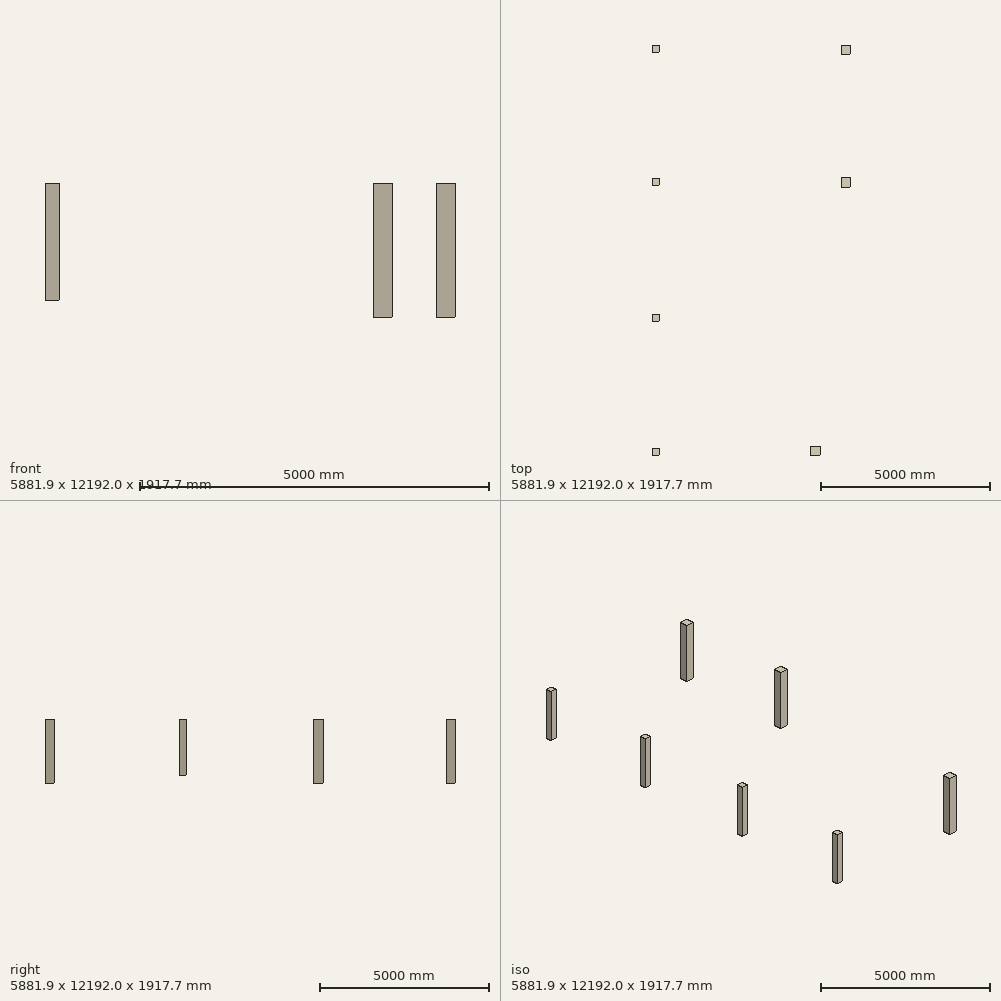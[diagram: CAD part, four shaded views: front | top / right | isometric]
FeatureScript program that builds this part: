
annotation { "Feature Type Name" : "Feature", "Feature Type Description" : "" }
export const myFeature = defineFeature(function(context is Context, id is Id, definition is map)
    precondition{}
    {
        {
            var Q0;
            Q0=qCreatedBy(makeId("Top.planeOp"),FACE);
            var sketch = newSketch(context, id + "F0", { "sketchPlane" : qUnion([Q0])});
            skLineSegment(sketch, "E0.bottom", {"start": v(0, 0) * mm, "end": v(203.2, 0) * mm});
            skLineSegment(sketch, "E0.top", {"start": v(0, 203.2) * mm, "end": v(203.2, 203.2) * mm});
            skLineSegment(sketch, "E0.left", {"start": v(0, 0) * mm, "end": v(0, 203.2) * mm});
            skLineSegment(sketch, "E0.right", {"start": v(203.2, 0) * mm, "end": v(203.2, 203.2) * mm});
            skSolve(sketch);
        }
        {
            var Q0;
            Q0=makeQuery(id+"F0.imprint","IMPRINT",FACE,{"disambiguationData":[TD([[makeQuery(id+"F0.imprint","IMPRINT",EDGE,{"derivedFrom":sQuery(id+"F0.wireOp",EDGE,"E0.bottom")}),1.0]])]});
            extrude(context, id + "F1", {"entities" : qUnion([Q0]), "depth" : 1676.4 * mm, "offsetDistance" : 25.4 * mm});
        }
        {
            var Q0;
            Q0=makeQuery(id+"F1.opExtrude","CAP_FACE",FACE,{"disambiguationData":[OSD([sQuery(id+"F0.wireOp",EDGE,"E0.bottom"),sQuery(id+"F0.wireOp",EDGE,"E0.top"),sQuery(id+"F0.wireOp",EDGE,"E0.left"),sQuery(id+"F0.wireOp",EDGE,"E0.right")])],"isStart":false});
            var sketch = newSketch(context, id + "F2", { "sketchPlane" : qUnion([Q0])});
            skLineSegment(sketch, "E1.bottom", {"start": v(0, 11988.8) * mm, "end": v(203.2, 11988.8) * mm});
            skLineSegment(sketch, "E1.top", {"start": v(0, 12192) * mm, "end": v(203.2, 12192) * mm});
            skLineSegment(sketch, "E1.left", {"start": v(0, 11988.8) * mm, "end": v(0, 12192) * mm});
            skLineSegment(sketch, "E1.right", {"start": v(203.2, 11988.8) * mm, "end": v(203.2, 12192) * mm});
            skSolve(sketch);
        }
        {
            var Q0;
            Q0=makeQuery(id+"F2.imprint","IMPRINT",FACE,{"disambiguationData":[TD([[makeQuery(id+"F2.imprint","IMPRINT",EDGE,{"derivedFrom":sQuery(id+"F2.wireOp",EDGE,"E1.bottom")}),1.0]])]});
            extrude(context, id + "F3", {"entities" : qUnion([Q0]), "oppositeDirection" : true, "depth" : 1676.4 * mm, "offsetDistance" : 25.4 * mm});
        }
        {
            var Q0;
            Q0=makeQuery(id+"F1.opExtrude","CAP_FACE",FACE,{"disambiguationData":[OSD([sQuery(id+"F0.wireOp",EDGE,"E0.bottom"),sQuery(id+"F0.wireOp",EDGE,"E0.top"),sQuery(id+"F0.wireOp",EDGE,"E0.left"),sQuery(id+"F0.wireOp",EDGE,"E0.right")])],"isStart":false});
            var sketch = newSketch(context, id + "F4", { "sketchPlane" : qUnion([Q0])});
            skLineSegment(sketch, "E2.bottom", {"start": v(0, 3975.1) * mm, "end": v(203.2, 3975.1) * mm});
            skLineSegment(sketch, "E2.top", {"start": v(0, 4178.3) * mm, "end": v(203.2, 4178.3) * mm});
            skLineSegment(sketch, "E2.left", {"start": v(0, 3975.1) * mm, "end": v(0, 4178.3) * mm});
            skLineSegment(sketch, "E2.right", {"start": v(203.2, 3975.1) * mm, "end": v(203.2, 4178.3) * mm});
            skSolve(sketch);
        }
        {
            var Q0;
            Q0=makeQuery(id+"F4.imprint","IMPRINT",FACE,{"disambiguationData":[TD([[makeQuery(id+"F4.imprint","IMPRINT",EDGE,{"derivedFrom":sQuery(id+"F4.wireOp",EDGE,"E2.bottom")}),1.0]])]});
            extrude(context, id + "F5", {"entities" : qUnion([Q0]), "oppositeDirection" : true, "depth" : 1676.4 * mm, "offsetDistance" : 25.4 * mm});
        }
        {
            var Q0;
            Q0=makeQuery(id+"F1.opExtrude","CAP_FACE",FACE,{"disambiguationData":[OSD([sQuery(id+"F0.wireOp",EDGE,"E0.bottom"),sQuery(id+"F0.wireOp",EDGE,"E0.top"),sQuery(id+"F0.wireOp",EDGE,"E0.left"),sQuery(id+"F0.wireOp",EDGE,"E0.right")])],"isStart":false});
            var sketch = newSketch(context, id + "F6", { "sketchPlane" : qUnion([Q0])});
            skLineSegment(sketch, "E3.bottom", {"start": v(0, 8039.1) * mm, "end": v(203.2, 8039.1) * mm});
            skLineSegment(sketch, "E3.top", {"start": v(0, 8242.3) * mm, "end": v(203.2, 8242.3) * mm});
            skLineSegment(sketch, "E3.left", {"start": v(0, 8039.1) * mm, "end": v(0, 8242.3) * mm});
            skLineSegment(sketch, "E3.right", {"start": v(203.2, 8039.1) * mm, "end": v(203.2, 8242.3) * mm});
            skSolve(sketch);
        }
        {
            var Q0;
            Q0=makeQuery(id+"F6.imprint","IMPRINT",FACE,{"disambiguationData":[TD([[makeQuery(id+"F6.imprint","IMPRINT",EDGE,{"derivedFrom":sQuery(id+"F6.wireOp",EDGE,"E3.bottom")}),1.0]])]});
            extrude(context, id + "F7", {"entities" : qUnion([Q0]), "oppositeDirection" : true, "depth" : 1676.4 * mm, "offsetDistance" : 25.4 * mm});
        }
        {
            var Q0;
            Q0=makeQuery(id+"F1.opExtrude","CAP_FACE",FACE,{"disambiguationData":[OSD([sQuery(id+"F0.wireOp",EDGE,"E0.bottom"),sQuery(id+"F0.wireOp",EDGE,"E0.top"),sQuery(id+"F0.wireOp",EDGE,"E0.left"),sQuery(id+"F0.wireOp",EDGE,"E0.right")])],"isStart":false});
            var sketch = newSketch(context, id + "F8", { "sketchPlane" : qUnion([Q0])});
            skLineSegment(sketch, "E4.bottom", {"start": v(4699, 0) * mm, "end": v(4978.4, 0) * mm});
            skLineSegment(sketch, "E4.top", {"start": v(4699, 279.4) * mm, "end": v(4978.4, 279.4) * mm});
            skLineSegment(sketch, "E4.left", {"start": v(4699, 0) * mm, "end": v(4699, 279.4) * mm});
            skLineSegment(sketch, "E4.right", {"start": v(4978.4, 0) * mm, "end": v(4978.4, 279.4) * mm});
            skSolve(sketch);
        }
        {
            var Q0;
            Q0=makeQuery(id+"F8.imprint","IMPRINT",FACE,{"disambiguationData":[TD([[makeQuery(id+"F8.imprint","IMPRINT",EDGE,{"derivedFrom":sQuery(id+"F8.wireOp",EDGE,"E4.bottom")}),1.0]])]});
            extrude(context, id + "F9", {"entities" : qUnion([Q0]), "oppositeDirection" : true, "depth" : 1917.7 * mm, "offsetDistance" : 25.4 * mm});
        }
        {
            var Q0;
            Q0=makeQuery(id+"F7.opExtrude","CAP_FACE",FACE,{"disambiguationData":[OSD([sQuery(id+"F6.wireOp",EDGE,"E3.bottom"),sQuery(id+"F6.wireOp",EDGE,"E3.top"),sQuery(id+"F6.wireOp",EDGE,"E3.left"),sQuery(id+"F6.wireOp",EDGE,"E3.right")])],"isStart":true});
            var sketch = newSketch(context, id + "F10", { "sketchPlane" : qUnion([Q0])});
            skLineSegment(sketch, "E5.bottom", {"start": v(5881.86, 12192) * mm, "end": v(5602.46, 12192) * mm});
            skLineSegment(sketch, "E5.top", {"start": v(5881.86, 11912.6) * mm, "end": v(5602.46, 11912.6) * mm});
            skLineSegment(sketch, "E5.left", {"start": v(5881.86, 12192) * mm, "end": v(5881.86, 11912.6) * mm});
            skLineSegment(sketch, "E5.right", {"start": v(5602.46, 12192) * mm, "end": v(5602.46, 11912.6) * mm});
            skSolve(sketch);
        }
        {
            var Q0;
            Q0=makeQuery(id+"F10.imprint","IMPRINT",FACE,{"disambiguationData":[TD([[makeQuery(id+"F10.imprint","IMPRINT",EDGE,{"derivedFrom":sQuery(id+"F10.wireOp",EDGE,"E5.bottom")}),1.0]])]});
            extrude(context, id + "F11", {"entities" : qUnion([Q0]), "oppositeDirection" : true, "depth" : 1917.7 * mm, "offsetDistance" : 25.4 * mm});
        }
        {
            var Q0;
            Q0=makeQuery(id+"F11.opExtrude","CAP_FACE",FACE,{"disambiguationData":[OSD([sQuery(id+"F10.wireOp",EDGE,"E5.bottom"),sQuery(id+"F10.wireOp",EDGE,"E5.top"),sQuery(id+"F10.wireOp",EDGE,"E5.left"),sQuery(id+"F10.wireOp",EDGE,"E5.right")])],"isStart":true});
            var sketch = newSketch(context, id + "F12", { "sketchPlane" : qUnion([Q0])});
            skLineSegment(sketch, "E6.bottom", {"start": v(5602.46, 8255) * mm, "end": v(5881.86, 8255) * mm});
            skLineSegment(sketch, "E6.top", {"start": v(5602.46, 7975.6) * mm, "end": v(5881.86, 7975.6) * mm});
            skLineSegment(sketch, "E6.left", {"start": v(5602.46, 8255) * mm, "end": v(5602.46, 7975.6) * mm});
            skLineSegment(sketch, "E6.right", {"start": v(5881.86, 8255) * mm, "end": v(5881.86, 7975.6) * mm});
            skSolve(sketch);
        }
        {
            var Q0;
            Q0=makeQuery(id+"F12.imprint","IMPRINT",FACE,{"disambiguationData":[TD([[makeQuery(id+"F12.imprint","IMPRINT",EDGE,{"derivedFrom":sQuery(id+"F12.wireOp",EDGE,"E6.bottom")}),-1.0]])]});
            extrude(context, id + "F13", {"entities" : qUnion([Q0]), "oppositeDirection" : true, "depth" : 1917.7 * mm, "offsetDistance" : 25.4 * mm});
        }
    });
